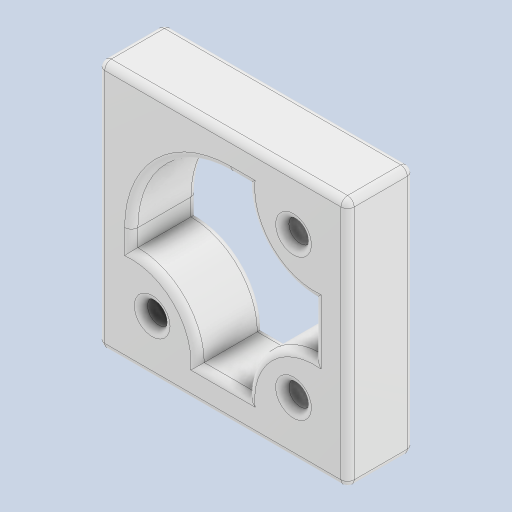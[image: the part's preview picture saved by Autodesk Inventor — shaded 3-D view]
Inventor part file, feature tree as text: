
AUTODESK INVENTOR PART (.ipt)
format: ipt  version: 2023 (Build 270158000, 158)  size: 332,288 bytes
history: native  units: mm
features: other x3, extrude x3, hole x1, pattern_circular x1, fillet x1
ambient origin geometry x8: Origin, YZ Plane, XZ Plane, XY Plane, X Axis, Y Axis, Z Axis, Center Point
bodies: Solid1 (feature_tree)
feature tree (9):
  other  "BaseWorkPlane"
  other  "Sk:Base"
  extrude  "Ex:Base"  Depth=10.0mm TaperAngle=0.0deg
  extrude  "Ex:ExtraForMirror"  Depth=0.15mm
  hole  "ThroughHole"  [1 undecoded]
  other  "Sk:ScrewRecess"
  extrude  "Ex:ScrewRecess"  Depth=27.6mm
  pattern_circular  "Pat:ScrewHoles"  [2 undecoded]
  fillet  "Fillet:Final"  Radius=13.8mm
note: 3 required parameter values undecoded (feature->parameter linkage not recoverable at this tier; creation-order binding heuristic only, values carry confidence <= 0.55)
